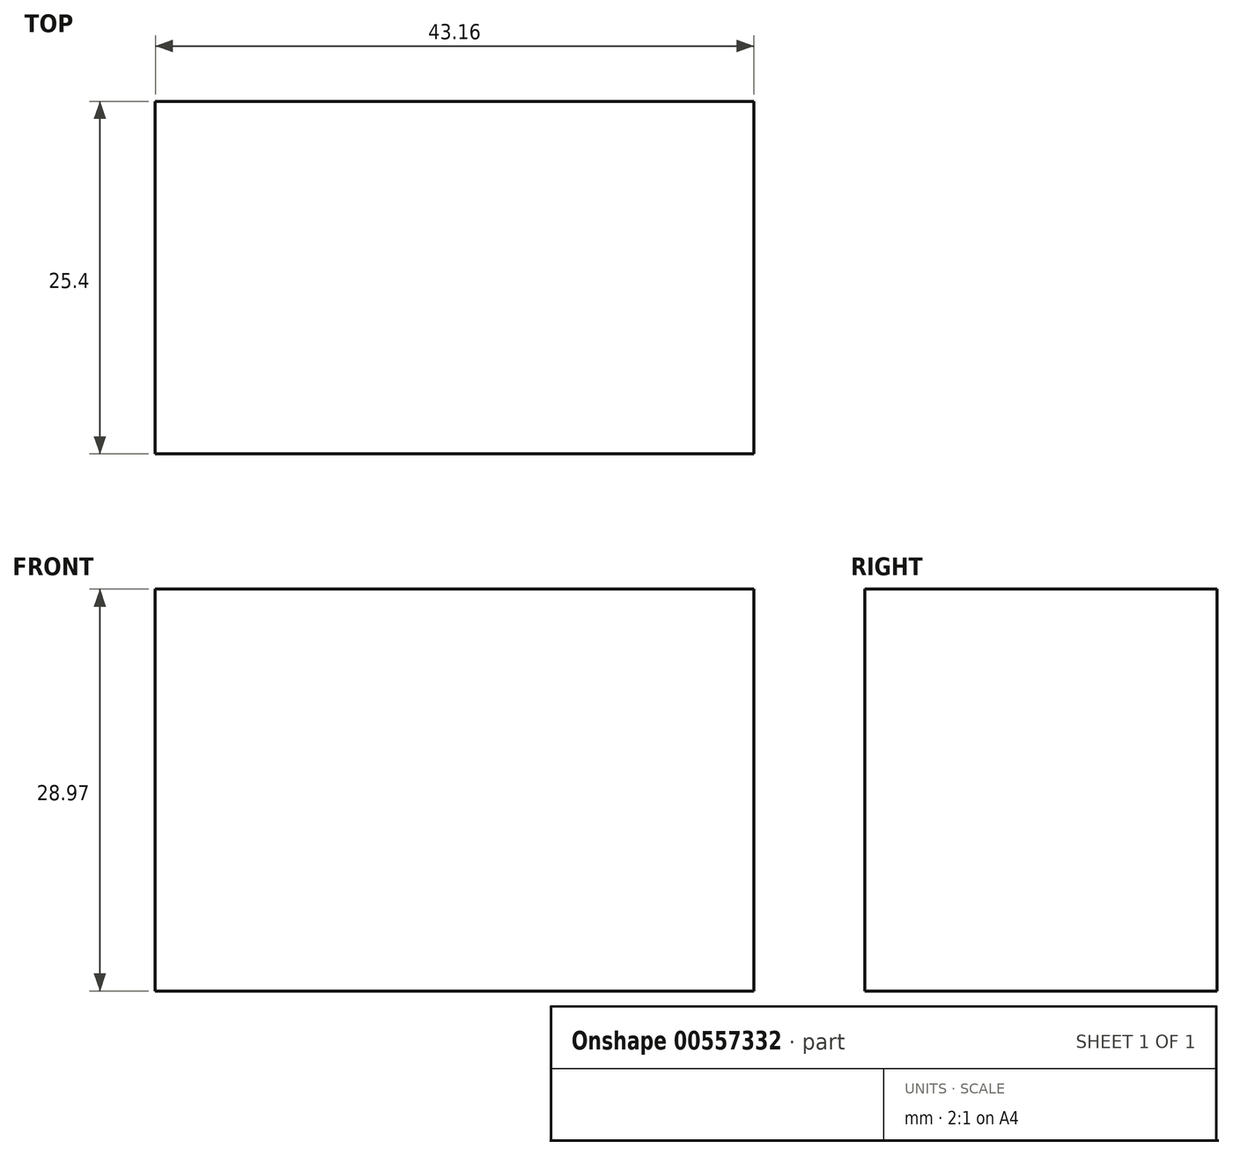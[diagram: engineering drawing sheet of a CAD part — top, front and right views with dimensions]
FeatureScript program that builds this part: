
annotation { "Feature Type Name" : "Feature", "Feature Type Description" : "" }
export const myFeature = defineFeature(function(context is Context, id is Id, definition is map)
    precondition{}
    {
        {
            var Q0;
            Q0=qCreatedBy(makeId("Front.planeOp"),FACE);
            var sketch = newSketch(context, id + "F0", { "sketchPlane" : qUnion([Q0])});
            skLineSegment(sketch, "E0.bottom", {"start": v(-103.42, 62.27) * mm, "end": v(-60.26, 62.27) * mm});
            skLineSegment(sketch, "E0.top", {"start": v(-103.42, 33.3) * mm, "end": v(-60.26, 33.3) * mm});
            skLineSegment(sketch, "E0.left", {"start": v(-103.42, 62.27) * mm, "end": v(-103.42, 33.3) * mm});
            skLineSegment(sketch, "E0.right", {"start": v(-60.26, 62.27) * mm, "end": v(-60.26, 33.3) * mm});
            skSolve(sketch);
        }
        {
            var Q0;
            Q0 = qSketchRegion(id + "F0", true);
            extrude(context, id + "F1", {"entities" : qUnion([Q0]), "depth" : 25.4 * mm, "offsetDistance" : 25.4 * mm});
        }
    });
